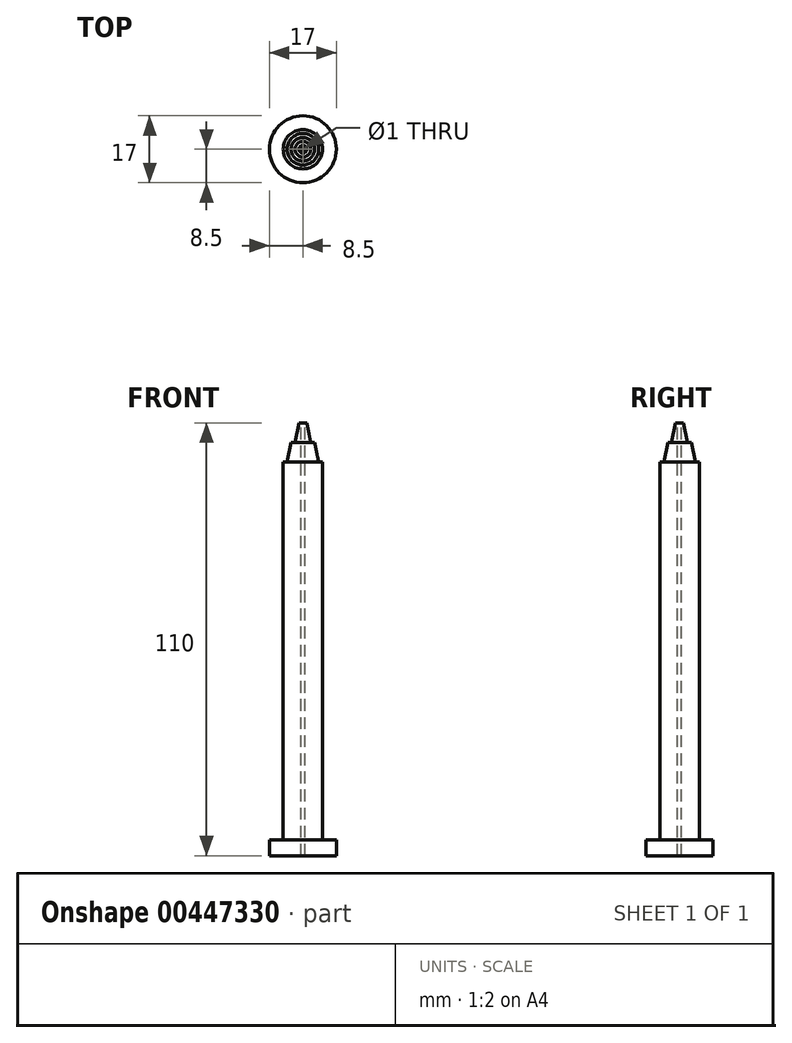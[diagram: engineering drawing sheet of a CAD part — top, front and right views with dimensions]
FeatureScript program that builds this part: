
annotation { "Feature Type Name" : "Feature", "Feature Type Description" : "" }
export const myFeature = defineFeature(function(context is Context, id is Id, definition is map)
    precondition{}
    {
        {
            var Q0;
            Q0=qCreatedBy(makeId("Top.planeOp"),FACE);
            var sketch = newSketch(context, id + "F0", { "sketchPlane" : qUnion([Q0])});
            skCircle(sketch, "E0", {"center": v(0, 0) * mm, "radius": 8.5 * mm});
            skSolve(sketch);
        }
        {
            var Q0;
            Q0=qSketchRegion(id+"F0",true);
            extrude(context, id + "F1", {"entities" : qUnion([Q0]), "depth" : 4 * mm});
        }
        {
            var Q0;
            Q0=qCreatedBy(makeId("Top.planeOp"),FACE);
            var sketch = newSketch(context, id + "F2", { "sketchPlane" : qUnion([Q0])});
            skCircle(sketch, "E1", {"center": v(0, 0) * mm, "radius": 5 * mm});
            skSolve(sketch);
        }
        {
            var Q0;
            Q0=qSketchRegion(id+"F2",true);
            extrude(context, id + "F3", {"entities" : qUnion([Q0]), "operationType" : NewBodyOperationType.ADD, "depth" : 100 * mm});
        }
        {
            var Q0;
            Q0=qCreatedBy(makeId("Right.planeOp"),FACE);
            var sketch = newSketch(context, id + "F4", { "sketchPlane" : qUnion([Q0])});
            skLineSegment(sketch, "E2", {"start": v(0, 105) * mm, "end": v(0, 100) * mm});
            skLineSegment(sketch, "E3", {"start": v(0, 100) * mm, "end": v(4, 100) * mm});
            skLineSegment(sketch, "E4", {"start": v(4, 100) * mm, "end": v(3, 105) * mm});
            skLineSegment(sketch, "E5", {"start": v(3, 105) * mm, "end": v(0, 105) * mm});
            skSolve(sketch);
        }
        {
            var Q0;
            Q0=makeQuery(id+"F4.imprint","IMPRINT",FACE,{"disambiguationData":[TD([[makeQuery(id+"F4.imprint","IMPRINT",EDGE,{"derivedFrom":sQuery(id+"F4.wireOp",EDGE,"E2")}),1.0]])]});
            var Q1;
            Q1=sQuery(id+"F4.wireOp",EDGE,"E2");
            revolve(context, id + "F5", {"operationType" : NewBodyOperationType.ADD, "entities" : qUnion([Q0]), "axis" : qUnion([Q1]), "revolveType" : RevolveType.FULL});
        }
        {
            var Q0;
            Q0=qCreatedBy(makeId("Right.planeOp"),FACE);
            var sketch = newSketch(context, id + "F6", { "sketchPlane" : qUnion([Q0])});
            skLineSegment(sketch, "E6", {"start": v(0, 110) * mm, "end": v(0, 105) * mm});
            skLineSegment(sketch, "E7", {"start": v(0, 105) * mm, "end": v(2, 105) * mm});
            skLineSegment(sketch, "E8", {"start": v(2, 105) * mm, "end": v(1, 110) * mm});
            skLineSegment(sketch, "E9", {"start": v(1, 110) * mm, "end": v(0, 110) * mm});
            skSolve(sketch);
        }
        {
            var Q0;
            Q0=makeQuery(id+"F6.imprint","IMPRINT",FACE,{"disambiguationData":[TD([[makeQuery(id+"F6.imprint","IMPRINT",EDGE,{"derivedFrom":sQuery(id+"F6.wireOp",EDGE,"E6")}),1.0]])]});
            var Q1;
            Q1=sQuery(id+"F6.wireOp",EDGE,"E6");
            revolve(context, id + "F7", {"operationType" : NewBodyOperationType.ADD, "entities" : qUnion([Q0]), "axis" : qUnion([Q1]), "revolveType" : RevolveType.FULL});
        }
        {
            var Q0;
            Q0=makeQuery(id+"F7.opRevolve","SWEPT_FACE",FACE,{"disambiguationData":[OSD([sQuery(id+"F6.wireOp",EDGE,"E9")])]});
            var sketch = newSketch(context, id + "F8", { "sketchPlane" : qUnion([Q0])});
            skCircle(sketch, "E10", {"center": v(0, 0) * mm, "radius": 0.5 * mm});
            skSolve(sketch);
        }
        {
            var Q0;
            Q0=makeQuery(id+"F8.imprint","IMPRINT",FACE,{"disambiguationData":[TD([[makeQuery(id+"F8.imprint","IMPRINT",EDGE,{"derivedFrom":sQuery(id+"F8.wireOp",EDGE,"E10")}),1.0]])]});
            extrude(context, id + "F9", {"entities" : qUnion([Q0]), "operationType" : NewBodyOperationType.REMOVE, "oppositeDirection" : true, "depth" : 125.6 * mm});
        }
    });
